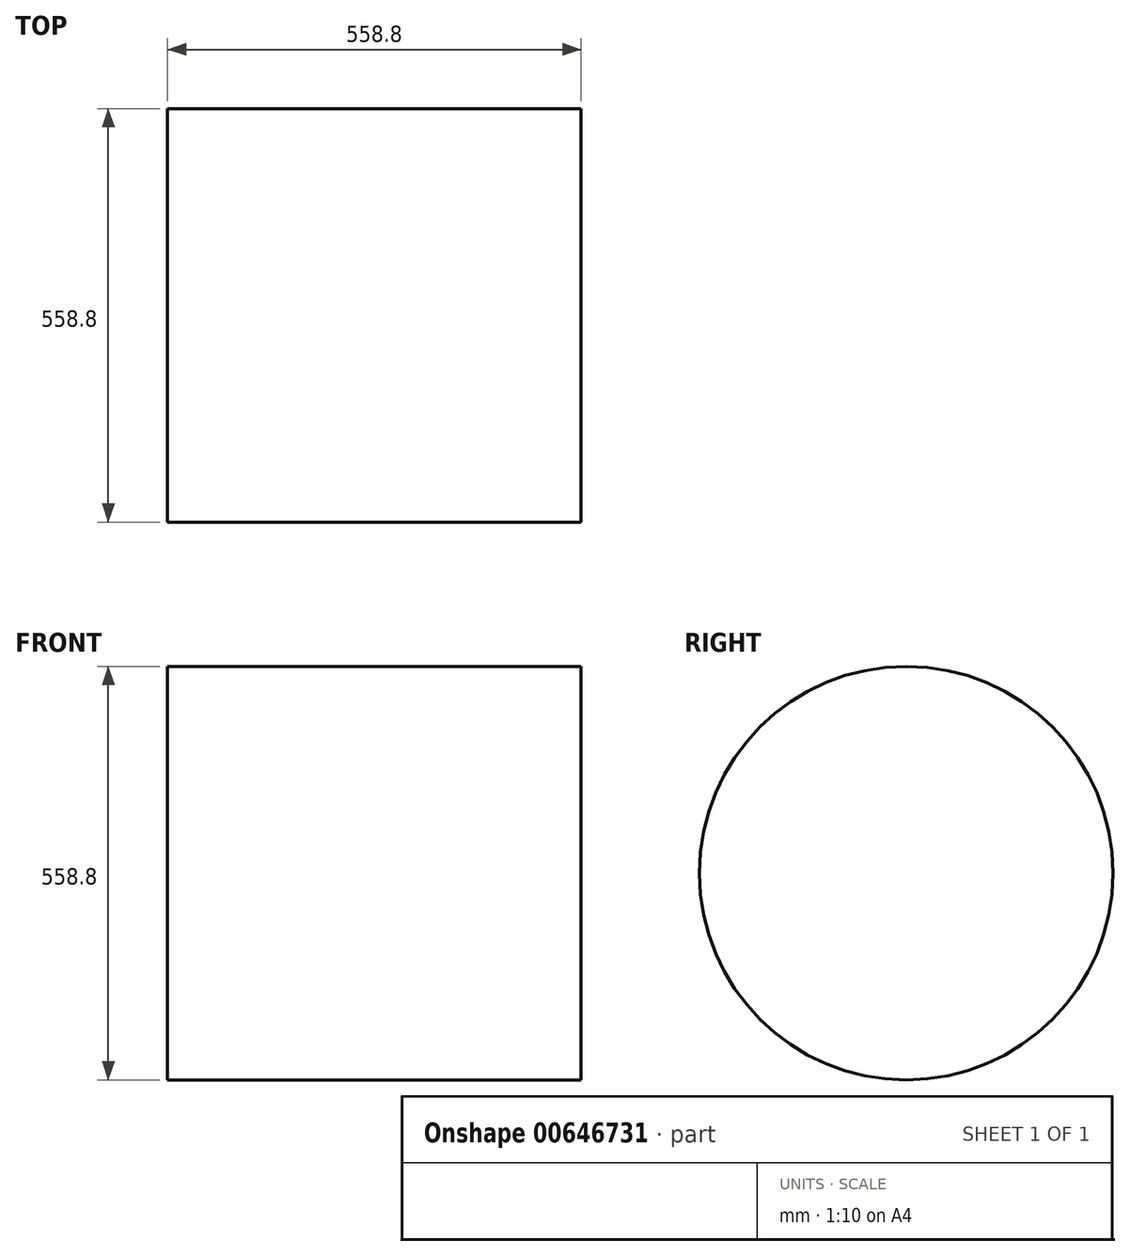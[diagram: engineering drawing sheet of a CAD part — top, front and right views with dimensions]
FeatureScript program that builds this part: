
annotation { "Feature Type Name" : "Feature", "Feature Type Description" : "" }
export const myFeature = defineFeature(function(context is Context, id is Id, definition is map)
    precondition{}
    {
        {
            var Q0;
            Q0=qCreatedBy(makeId("Right.planeOp"),FACE);
            var sketch = newSketch(context, id + "F0", { "sketchPlane" : qUnion([Q0])});
            skCircle(sketch, "E0", {"center": v(-8.78, 24.9) * mm, "radius": 279.4 * mm});
            skSolve(sketch);
        }
        {
            var Q0;
            Q0=makeQuery(id+"F0.imprint","IMPRINT",FACE,{"disambiguationData":[TD([[makeQuery(id+"F0.imprint","IMPRINT",EDGE,{"derivedFrom":sQuery(id+"F0.wireOp",EDGE,"E0")}),1.0]])]});
            extrude(context, id + "F1", {"entities" : qUnion([Q0]), "depth" : 558.8 * mm, "offsetDistance" : 25.4 * mm});
        }
    });
